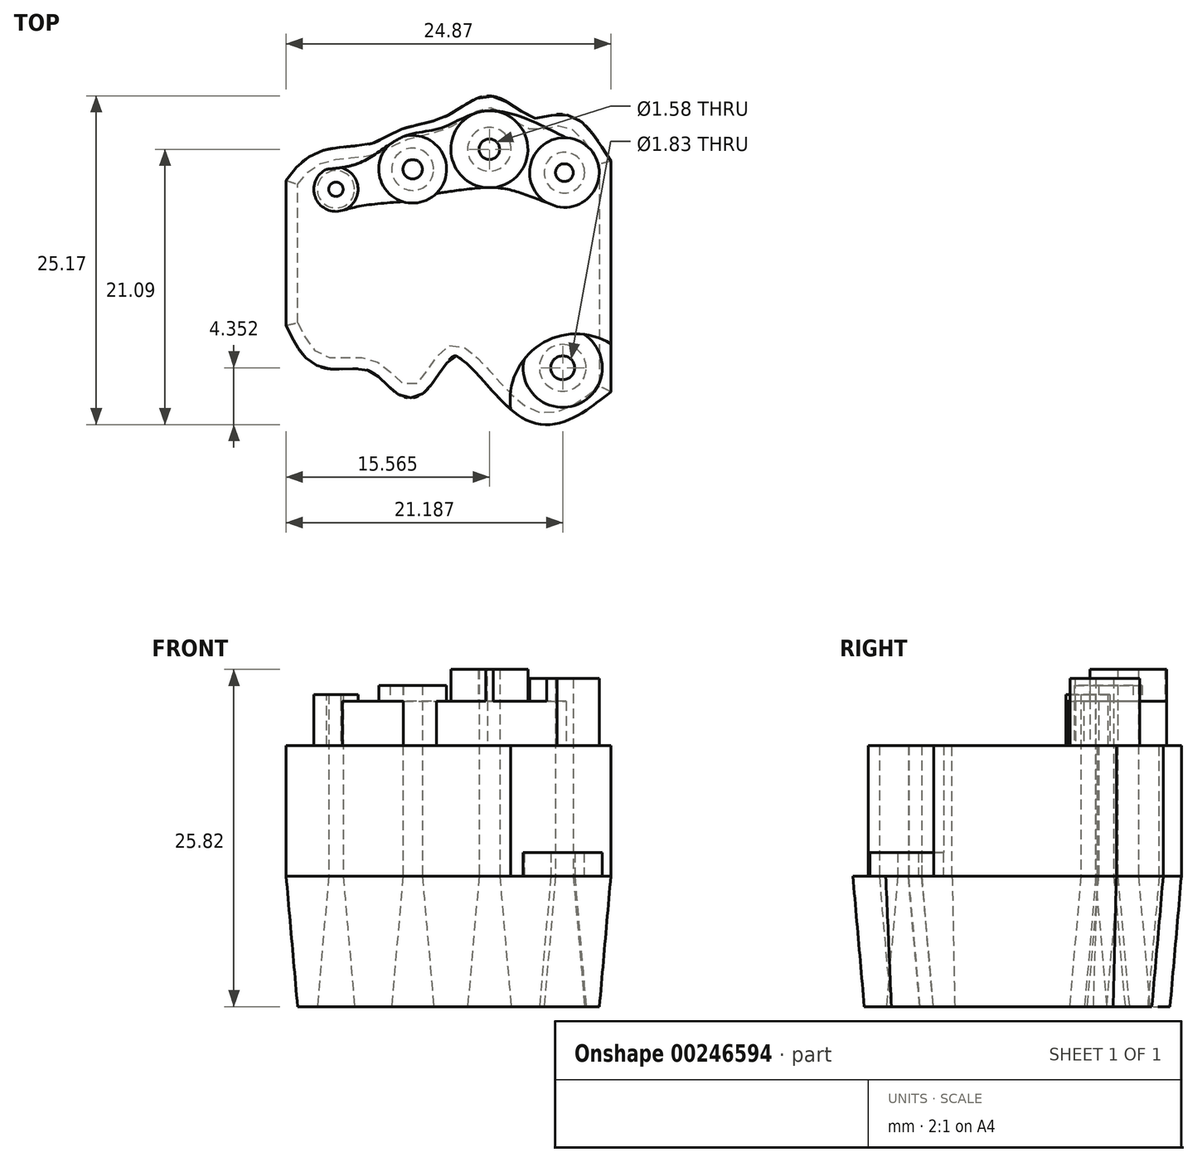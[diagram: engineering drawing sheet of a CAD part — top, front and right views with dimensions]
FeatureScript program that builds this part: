
annotation { "Feature Type Name" : "Feature", "Feature Type Description" : "" }
export const myFeature = defineFeature(function(context is Context, id is Id, definition is map)
    precondition{}
    {
        {
            var Q0;
            Q0=qCreatedBy(makeId("Top.planeOp"),FACE);
            var sketch = newSketch(context, id + "F0", { "sketchPlane" : qUnion([Q0])});
            skLineSegment(sketch, "E0", {"start": v(-49.17, 30.08) * mm, "end": v(-49.17, 19.47) * mm});
            skLineSegment(sketch, "E1", {"start": v(-26.04, 14.62) * mm, "end": v(-26.04, 31.61) * mm});
            skFitSpline(sketch, "E2", {"points": [v(-49.17, 30.08) * mm, v(-47.25, 31.74) * mm, v(-43.16, 32.38) * mm, v(-41.12, 33.4) * mm, v(-37.29, 34.55) * mm, v(-34.35, 35.95) * mm, v(-31.28, 34.3) * mm, v(-28.72, 34.55) * mm, v(-26.04, 31.61) * mm], "startDerivative": vector(13.71, 18) * mm, "endDerivative": vector(18.42, -29.74) * mm});
            skFitSpline(sketch, "E3", {"points": [v(-49.17, 19.47) * mm, v(-47.12, 16.92) * mm, v(-43.16, 16.53) * mm, v(-40.35, 14.62) * mm, v(-37.29, 17.81) * mm, v(-31.28, 12.83) * mm, v(-26.04, 14.62) * mm], "startDerivative": vector(11.38, -23.82) * mm, "endDerivative": vector(28.32, 22) * mm});
            skCircle(sketch, "E4", {"center": v(-46.23, 29.7) * mm, "radius": 1.43 * mm});
            skCircle(sketch, "E5", {"center": v(-40.35, 31.23) * mm, "radius": 1.62 * mm});
            skCircle(sketch, "E6", {"center": v(-34.47, 32.76) * mm, "radius": 1.67 * mm});
            skCircle(sketch, "E7", {"center": v(-28.72, 30.97) * mm, "radius": 1.55 * mm});
            skCircle(sketch, "E8", {"center": v(-28.85, 16.02) * mm, "radius": 1.79 * mm});
            skSolve(sketch);
        }
        {
            var Q0;
            Q0=makeQuery(id+"F0.imprint","IMPRINT",FACE,{"disambiguationData":[TD([[makeQuery(id+"F0.imprint","IMPRINT",EDGE,{"derivedFrom":sQuery(id+"F0.wireOp",EDGE,"E0")}),1.0]])]});
            extrude(context, id + "F1", {"entities" : qUnion([Q0]), "depth" : 10 * mm, "hasDraft" : true, "draftAngle" : 5 * degree});
        }
        {
            var Q0;
            Q0=makeQuery(id+"F1.opExtrude","CAP_FACE",FACE,{"disambiguationData":[OSD([sQuery(id+"F0.wireOp",EDGE,"E0"),sQuery(id+"F0.wireOp",EDGE,"E1"),sQuery(id+"F0.wireOp",EDGE,"E2"),sQuery(id+"F0.wireOp",EDGE,"E3"),sQuery(id+"F0.wireOp",EDGE,"E4"),sQuery(id+"F0.wireOp",EDGE,"E5"),sQuery(id+"F0.wireOp",EDGE,"E6"),sQuery(id+"F0.wireOp",EDGE,"E7"),sQuery(id+"F0.wireOp",EDGE,"E8")])],"isStart":false});
            var sketch = newSketch(context, id + "F2", { "sketchPlane" : qUnion([Q0])});
            skArc(sketch, "E9", {"start": v(-25.17, 17.86) * mm, "mid": v(-30.6, 17.8) * mm, "end": v(-32.83, 12.84) * mm});
            skLineSegment(sketch, "E10", {"start": v(-50.04, 30.37) * mm, "end": v(-50.04, 19.27) * mm});
            skSolve(sketch);
        }
        {
            var Q0;
            {var subQ2=sQuery(id+"F2.wireOp",EDGE,"E9");Q0=makeQuery(id+"F2.imprint","IMPRINT",FACE,{"disambiguationData":[TD([[makeQuery(id+"F2.imprint","IMPRINT",EDGE,{"derivedFrom":subQ2}),-1.0]])]});}
            extrude(context, id + "F3", {"entities" : qUnion([Q0]), "operationType" : NewBodyOperationType.ADD, "depth" : 10 * mm});
        }
        {
            var Q0;
            Q0=makeQuery(id+"F3.opExtrude","CAP_FACE",FACE,{"disambiguationData":[OSD([sQuery(id+"F0.wireOp",EDGE,"E1"),sQuery(id+"F0.wireOp",EDGE,"E2"),sQuery(id+"F0.wireOp",EDGE,"E3"),sQuery(id+"F0.wireOp",EDGE,"E4"),sQuery(id+"F0.wireOp",EDGE,"E5"),sQuery(id+"F0.wireOp",EDGE,"E6"),sQuery(id+"F0.wireOp",EDGE,"E7"),sQuery(id+"F2.wireOp",EDGE,"E9"),sQuery(id+"F2.wireOp",EDGE,"E10")])],"isStart":false});
            var sketch = newSketch(context, id + "F4", { "sketchPlane" : qUnion([Q0])});
            skCircle(sketch, "E11", {"center": v(-46.23, 29.7) * mm, "radius": 1.7 * mm});
            skCircle(sketch, "E12", {"center": v(-40.35, 31.23) * mm, "radius": 2.6 * mm});
            skCircle(sketch, "E13", {"center": v(-34.47, 32.76) * mm, "radius": 2.95 * mm});
            skCircle(sketch, "E14", {"center": v(-28.72, 30.97) * mm, "radius": 2.67 * mm});
            skFitSpline(sketch, "E15", {"points": [v(-45.72, 28.08) * mm, v(-44.16, 28.44) * mm, v(-41.08, 28.74) * mm], "startDerivative": vector(3.4, 0.96) * mm, "endDerivative": vector(5.75, 0.37) * mm});
            skFitSpline(sketch, "E16", {"points": [v(-38.54, 29.37) * mm, v(-37.35, 29.55) * mm, v(-34.17, 29.82) * mm, v(-31.9, 29.35) * mm, v(-29.3, 28.36) * mm], "startDerivative": vector(5.61, 0.85) * mm, "endDerivative": vector(9.81, -3.88) * mm});
            skFitSpline(sketch, "E17", {"points": [v(-46.95, 31.23) * mm, v(-44.1, 31.86) * mm, v(-41.05, 33.72) * mm, v(-38.13, 34.41) * mm, v(-34.62, 35.71) * mm, v(-28.6, 33.64) * mm], "startDerivative": vector(16.57, 1.56) * mm, "endDerivative": vector(25, -12.83) * mm});
            skSolve(sketch);
        }
        {
            var Q0;
            {var subQ0=sQuery(id+"F4.wireOp",EDGE,"E15");Q0=makeQuery(id+"F4.imprint","IMPRINT",FACE,{"disambiguationData":[TD([[makeQuery(id+"F4.imprint","IMPRINT",EDGE,{"derivedFrom":subQ0}),1.0]])]});}
            var Q1;
            {var subQ0=sQuery(id+"F4.wireOp",EDGE,"E16");var subQ1=sQuery(id+"F4.wireOp",EDGE,"E12");var subQ2=makeQuery(id+"F4.imprint","INTERSECT",VERTEX,{"derivedFrom":[subQ1,subQ0]});Q1=makeQuery(id+"F4.imprint","IMPRINT",FACE,{"disambiguationData":[TD([[makeQuery(id+"F4.imprint","IMPRINT",EDGE,{"disambiguationData":[TD([[subQ2,-1.0]])],"derivedFrom":subQ1}),-1.0]])]});}
            var Q2;
            {var subQ0=sQuery(id+"F4.wireOp",EDGE,"E17");var subQ1=sQuery(id+"F4.wireOp",EDGE,"E13");var subQ2=makeQuery(id+"F4.imprint","INTERSECT",VERTEX,{"disambiguationData":[OD(1.0)],"derivedFrom":[subQ1,subQ0]});Q2=makeQuery(id+"F4.imprint","IMPRINT",FACE,{"disambiguationData":[TD([[makeQuery(id+"F4.imprint","IMPRINT",EDGE,{"disambiguationData":[TD([[subQ2,1.0]])],"derivedFrom":subQ1}),-1.0]])]});}
            extrude(context, id + "F5", {"entities" : qUnion([Q0, Q1, Q2]), "operationType" : NewBodyOperationType.ADD, "depth" : 3.4 * mm});
        }
        {
            var Q0;
            Q0=makeQuery(id+"F4.imprint","IMPRINT",FACE,{"disambiguationData":[TD([[makeQuery(id+"F4.imprint","IMPRINT",EDGE,{"derivedFrom":makeQuery(id+"F3.opExtrude","CAP_EDGE",EDGE,{"disambiguationData":[OSD([sQuery(id+"F0.wireOp",EDGE,"E7")])],"isStart":false})}),-1.0]])]});
            var Q1;
            Q1=makeQuery(id+"F4.imprint","IMPRINT",FACE,{"disambiguationData":[TD([[makeQuery(id+"F4.imprint","IMPRINT",EDGE,{"derivedFrom":makeQuery(id+"F3.opExtrude","CAP_EDGE",EDGE,{"disambiguationData":[OSD([sQuery(id+"F0.wireOp",EDGE,"E4")])],"isStart":false})}),-1.0]])]});
            var Q2;
            Q2=makeQuery(id+"F4.imprint","IMPRINT",FACE,{"disambiguationData":[TD([[makeQuery(id+"F4.imprint","IMPRINT",EDGE,{"derivedFrom":makeQuery(id+"F3.opExtrude","CAP_EDGE",EDGE,{"disambiguationData":[OSD([sQuery(id+"F0.wireOp",EDGE,"E5")])],"isStart":false})}),-1.0]])]});
            var Q3;
            Q3=makeQuery(id+"F4.imprint","IMPRINT",FACE,{"disambiguationData":[TD([[makeQuery(id+"F4.imprint","IMPRINT",EDGE,{"derivedFrom":makeQuery(id+"F3.opExtrude","CAP_EDGE",EDGE,{"disambiguationData":[OSD([sQuery(id+"F0.wireOp",EDGE,"E6")])],"isStart":false})}),-1.0]])]});
            extrude(context, id + "F6", {"entities" : qUnion([Q0, Q1, Q2, Q3]), "operationType" : NewBodyOperationType.ADD, "depth" : 3.9 * mm});
        }
        {
            var Q0;
            Q0=makeQuery(id+"F6.opExtrude","CAP_FACE",FACE,{"disambiguationData":[OSD([sQuery(id+"F0.wireOp",EDGE,"E5"),sQuery(id+"F4.wireOp",EDGE,"E12"),sQuery(id+"F4.wireOp",EDGE,"E17")])],"isStart":false});
            var Q1;
            Q1=makeQuery(id+"F6.opExtrude","CAP_FACE",FACE,{"disambiguationData":[OSD([sQuery(id+"F0.wireOp",EDGE,"E6"),sQuery(id+"F4.wireOp",EDGE,"E13"),sQuery(id+"F4.wireOp",EDGE,"E16"),sQuery(id+"F4.wireOp",EDGE,"E17")])],"isStart":false});
            var Q2;
            Q2=makeQuery(id+"F6.opExtrude","CAP_FACE",FACE,{"disambiguationData":[OSD([sQuery(id+"F0.wireOp",EDGE,"E7"),sQuery(id+"F4.wireOp",EDGE,"E14"),sQuery(id+"F4.wireOp",EDGE,"E16")])],"isStart":false});
            extrude(context, id + "F7", {"entities" : qUnion([Q0, Q1, Q2]), "operationType" : NewBodyOperationType.ADD, "depth" : 0.7 * mm});
        }
        {
            var Q0;
            Q0=makeQuery(id+"F7.opExtrude","CAP_FACE",FACE,{"disambiguationData":[OSD([sQuery(id+"F0.wireOp",EDGE,"E6"),sQuery(id+"F4.wireOp",EDGE,"E13"),sQuery(id+"F4.wireOp",EDGE,"E16"),sQuery(id+"F4.wireOp",EDGE,"E17")])],"isStart":false});
            var Q1;
            Q1=makeQuery(id+"F7.opExtrude","CAP_FACE",FACE,{"disambiguationData":[OSD([sQuery(id+"F0.wireOp",EDGE,"E7"),sQuery(id+"F4.wireOp",EDGE,"E14"),sQuery(id+"F4.wireOp",EDGE,"E16")])],"isStart":false});
            extrude(context, id + "F8", {"entities" : qUnion([Q0, Q1]), "operationType" : NewBodyOperationType.ADD, "depth" : 0.52 * mm});
        }
        {
            var Q0;
            Q0=makeQuery(id+"F8.opExtrude","CAP_FACE",FACE,{"disambiguationData":[OSD([sQuery(id+"F0.wireOp",EDGE,"E6"),sQuery(id+"F4.wireOp",EDGE,"E13"),sQuery(id+"F4.wireOp",EDGE,"E16"),sQuery(id+"F4.wireOp",EDGE,"E17")])],"isStart":false});
            extrude(context, id + "F9", {"entities" : qUnion([Q0]), "operationType" : NewBodyOperationType.ADD, "depth" : 0.7 * mm});
        }
        {
            var Q0;
            Q0=makeQuery(id+"F1.opExtrude","CAP_FACE",FACE,{"disambiguationData":[OSD([sQuery(id+"F0.wireOp",EDGE,"E0"),sQuery(id+"F0.wireOp",EDGE,"E1"),sQuery(id+"F0.wireOp",EDGE,"E2"),sQuery(id+"F0.wireOp",EDGE,"E3"),sQuery(id+"F0.wireOp",EDGE,"E4"),sQuery(id+"F0.wireOp",EDGE,"E5"),sQuery(id+"F0.wireOp",EDGE,"E6"),sQuery(id+"F0.wireOp",EDGE,"E7"),sQuery(id+"F0.wireOp",EDGE,"E8")])],"isStart":false});
            var sketch = newSketch(context, id + "F10", { "sketchPlane" : qUnion([Q0])});
            skCircle(sketch, "E18", {"center": v(-28.85, 16.02) * mm, "radius": 3.03 * mm});
            skSolve(sketch);
        }
        {
            var Q0;
            Q0=makeQuery(id+"F10.imprint","IMPRINT",FACE,{"disambiguationData":[TD([[makeQuery(id+"F10.imprint","IMPRINT",EDGE,{"derivedFrom":makeQuery(id+"F1.opExtrude","CAP_EDGE",EDGE,{"disambiguationData":[OSD([sQuery(id+"F0.wireOp",EDGE,"E8")])],"isStart":false})}),-1.0]])]});
            extrude(context, id + "F11", {"entities" : qUnion([Q0]), "operationType" : NewBodyOperationType.ADD, "depth" : 1.8 * mm});
        }
    });
